# Revit family: RB bjælker Spæncom
name_source: partatom
category: Structural Framing
revit_build: Autodesk Revit 2014 (Build: 20130308_1515(x64)
units: mm (PartAtom-declared; Revit-internal decimal feet)

## types (28) — shared parameters
Manufacturer = Spæncom

## per-type parameters (varying)
| type | Height element | Width element |
| RB18/36 | 360 mm  [stored 1.1811 ft] | 180 mm  [stored 0.590551 ft] |
| RB18/42 | 420 mm  [stored 1.37795 ft] | 180 mm  [stored 0.590551 ft] |
| RB18/48 | 480 mm  [stored 1.5748 ft] | 180 mm  [stored 0.590551 ft] |
| RB18/54 | 540 mm  [stored 1.77165 ft] | 180 mm  [stored 0.590551 ft] |
| RB24/48 | 480 mm  [stored 1.5748 ft] | 240 mm  [stored 0.787402 ft] |
| RB24/54 | 540 mm  [stored 1.77165 ft] | 240 mm  [stored 0.787402 ft] |
| RB24/60 | 600 mm | 240 mm  [stored 0.787402 ft] |
| RB24/66 | 660 mm  [stored 2.16535 ft] | 240 mm  [stored 0.787402 ft] |
| RB30/60 | 600 mm | 300 mm |
| RB30/66 | 660 mm  [stored 2.16535 ft] | 300 mm |
| RB30/72 | 720 mm  [stored 2.3622 ft] | 300 mm |
| RB36/60 | 600 mm | 360 mm  [stored 1.1811 ft] |
| RB36/66 | 660 mm  [stored 2.16535 ft] | 360 mm  [stored 1.1811 ft] |
| RB36/72 | 720 mm  [stored 2.3622 ft] | 360 mm  [stored 1.1811 ft] |
| RB36/84 | 840 mm  [stored 2.75591 ft] | 360 mm  [stored 1.1811 ft] |
| RB36/110 | 1100 mm | 360 mm  [stored 1.1811 ft] |
| RB42/60 | 600 mm | 420 mm  [stored 1.37795 ft] |
| RB42/66 | 660 mm  [stored 2.16535 ft] | 420 mm  [stored 1.37795 ft] |
| RB42/72 | 720 mm  [stored 2.3622 ft] | 420 mm  [stored 1.37795 ft] |
| RB42/84 | 840 mm  [stored 2.75591 ft] | 420 mm  [stored 1.37795 ft] |
| RB42/110 | 1100 mm | 420 mm  [stored 1.37795 ft] |
| RB42/140 | 1400 mm  [stored 4.59318 ft] | 420 mm  [stored 1.37795 ft] |
| RB50/60 | 600 mm | 500 mm  [stored 1.64042 ft] |
| RB50/66 | 660 mm  [stored 2.16535 ft] | 500 mm  [stored 1.64042 ft] |
| RB50/72 | 720 mm  [stored 2.3622 ft] | 500 mm  [stored 1.64042 ft] |
| RB50/84 | 840 mm  [stored 2.75591 ft] | 500 mm  [stored 1.64042 ft] |
| RB50/110 | 1100 mm | 500 mm  [stored 1.64042 ft] |
| RB50/140 | 1400 mm  [stored 4.59318 ft] | 500 mm  [stored 1.64042 ft] |

note: column(s) folded — value = type name in every type: Model

note: [stored X ft] marks values corroborated as IEEE doubles in the binary element streams (Revit-internal decimal feet)

## geometry (parser evidence)
native form markers: Sweep x6
no freeform markers — native parametric forms only
